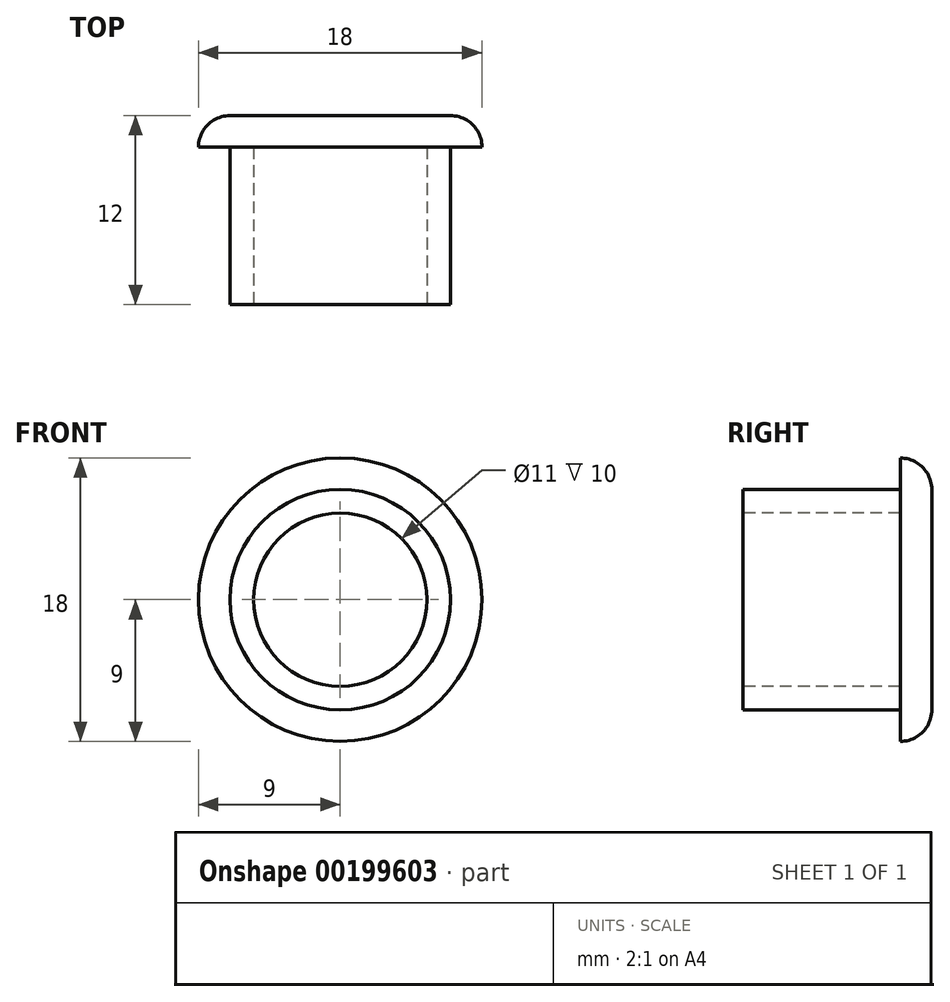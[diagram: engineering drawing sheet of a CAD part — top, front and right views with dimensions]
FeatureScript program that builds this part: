
annotation { "Feature Type Name" : "Feature", "Feature Type Description" : "" }
export const myFeature = defineFeature(function(context is Context, id is Id, definition is map)
    precondition{}
    {
        {
            var Q0;
            Q0=qCreatedBy(makeId("Front.planeOp"),FACE);
            var sketch = newSketch(context, id + "F0", { "sketchPlane" : qUnion([Q0])});
            skCircle(sketch, "E0", {"center": v(0, 0) * mm, "radius": 9 * mm});
            skSolve(sketch);
        }
        {
            var Q0;
            Q0 = qSketchRegion(id + "F0", true);
            extrude(context, id + "F1", {"entities" : qUnion([Q0]), "depth" : 12 * mm});
        }
        {
            var Q0;
            Q0=makeQuery(id+"F1.opExtrude","CAP_FACE",FACE,{"disambiguationData":[OSD([sQuery(id+"F0.wireOp",EDGE,"E0")])],"isStart":false});
            var sketch = newSketch(context, id + "F2", { "sketchPlane" : qUnion([Q0])});
            skCircle(sketch, "E1", {"center": v(0, 0) * mm, "radius": 7 * mm});
            skSolve(sketch);
        }
        {
            var Q0;
            Q0=makeQuery(id+"F2.imprint","IMPRINT",FACE,{"disambiguationData":[TD([[makeQuery(id+"F2.imprint","IMPRINT",EDGE,{"derivedFrom":sQuery(id+"F2.wireOp",EDGE,"E1")}),-1.0]])]});
            extrude(context, id + "F3", {"entities" : qUnion([Q0]), "operationType" : NewBodyOperationType.REMOVE, "oppositeDirection" : true, "depth" : 10 * mm});
        }
        {
            var Q0;
            Q0=makeQuery(id+"F1.opExtrude","CAP_FACE",FACE,{"disambiguationData":[OSD([sQuery(id+"F0.wireOp",EDGE,"E0")])],"isStart":false});
            var sketch = newSketch(context, id + "F4", { "sketchPlane" : qUnion([Q0])});
            skCircle(sketch, "E2", {"center": v(0, 0) * mm, "radius": 5.5 * mm});
            skSolve(sketch);
        }
        {
            var Q0;
            Q0 = qSketchRegion(id + "F4", true);
            extrude(context, id + "F5", {"entities" : qUnion([Q0]), "operationType" : NewBodyOperationType.REMOVE, "oppositeDirection" : true, "depth" : 10 * mm});
        }
        {
            var Q0;
            Q0=makeQuery(id+"F1.opExtrude","CAP_FACE",FACE,{"disambiguationData":[OSD([sQuery(id+"F0.wireOp",EDGE,"E0")])],"isStart":true});
            fillet(context, id + "F6", {"entities" : qUnion([Q0]), "radius" : 2 * mm, "tangentPropagation" : true, "allowEdgeOverflow" : false});
        }
    });
